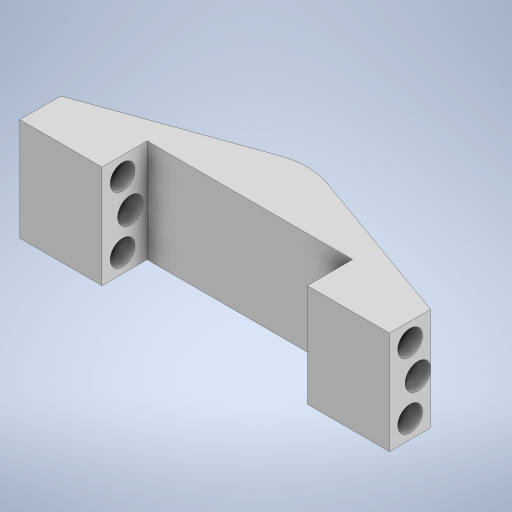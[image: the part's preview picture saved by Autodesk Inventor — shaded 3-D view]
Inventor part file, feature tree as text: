
AUTODESK INVENTOR PART (.ipt)
format: ipt  version: 2024 (Build 280153000, 153)  size: 263,680 bytes
history: native  units: mm
features: sketch x5, extrude x3, hole x2
ambient origin geometry x8: Origin, YZ Plane, XZ Plane, XY Plane, X Axis, Y Axis, Z Axis, Center Point
bodies: Volumenkörper1 (feature_tree)
feature tree (10):
  extrude  "Extrusion1"  Depth=15.0mm
  extrude  "Extrusion4"  Depth=25.0mm TaperAngle=0.0deg
  hole  "Bohrung1"  [1 undecoded]
  hole  "Bohrung2"  [1 undecoded]
  extrude  "Extrusion5"  Depth=25.0mm
  sketch  "Skizze1"  dims[d2=35.0mm d3=15.0mm]
  sketch  "Skizze4"  dims[d4=45.0mm d5=25.0mm d6=0.0mm]
  sketch  "Skizze5"  dims[d15=10.0mm d16=0.0mm d17=5.0mm]
  sketch  "Skizze6"  dims[d18=5.0mm d19=25.0mm]
  sketch  "Skizze7"  dims[d20=16.0mm d21=4.5mm d22=6.0mm d23=6.0mm d24=4.0mm d25=2.0mm d26=90.0deg d27=8.0mm d28=20.594885mm d29=3.1mm d30=12.5mm d31=6.2mm d32=6.0mm d33=4.0mm d34=2.0mm d35=90.0deg d36=8.0mm d37=20.594885mm d38=50.0mm d39=11.0mm d40=25.0mm d41=0.0mm]
note: 2 required parameter values undecoded (feature->parameter linkage not recoverable at this tier; creation-order binding heuristic only, values carry confidence <= 0.55)
